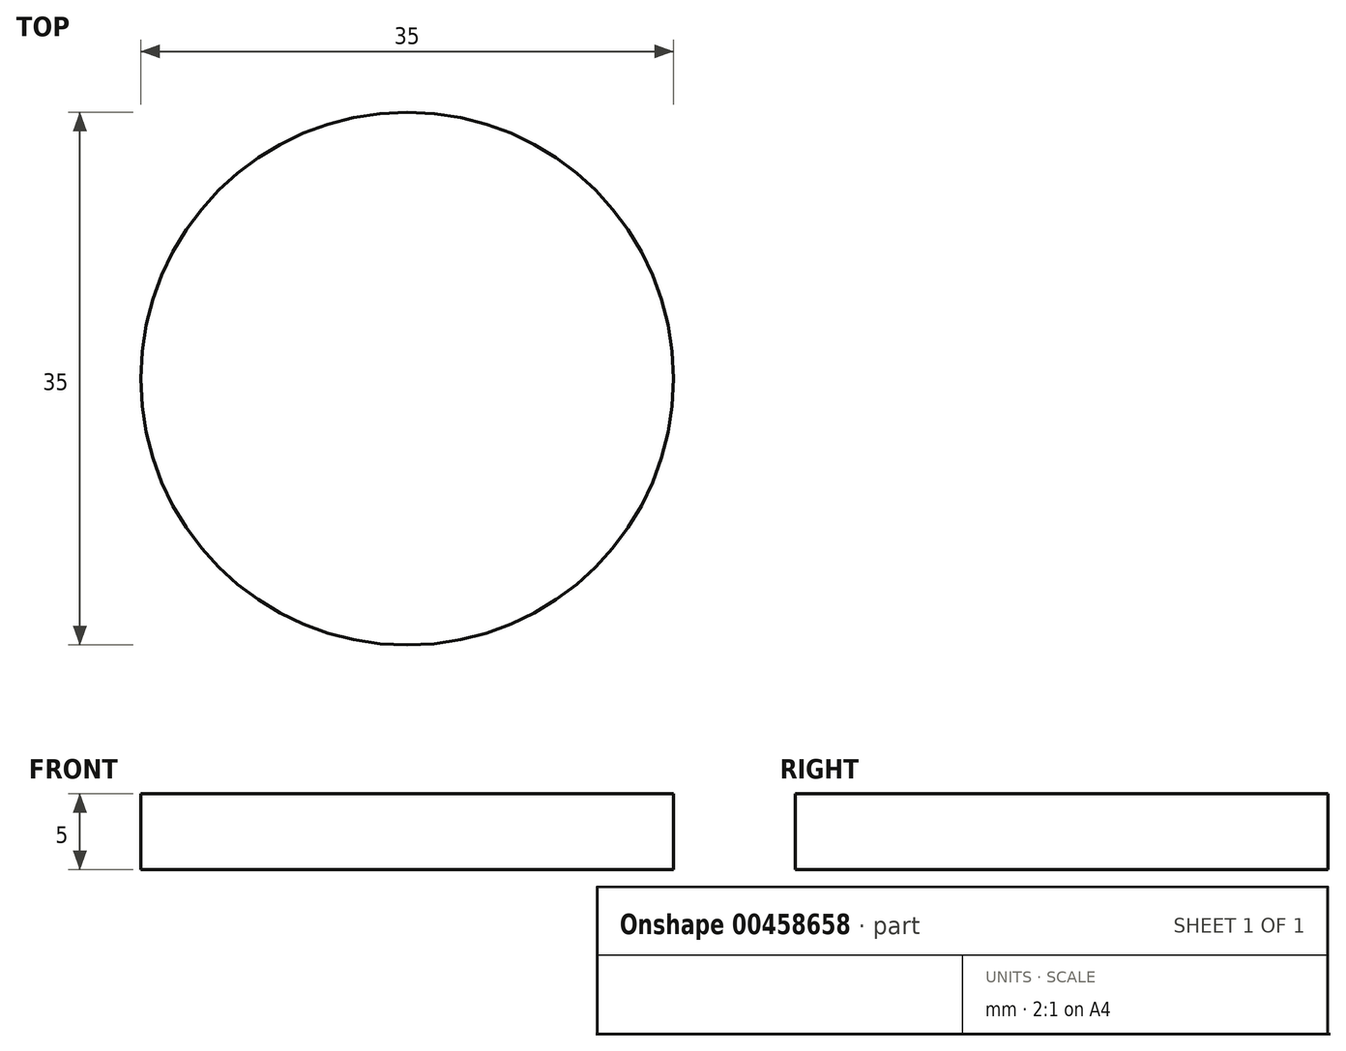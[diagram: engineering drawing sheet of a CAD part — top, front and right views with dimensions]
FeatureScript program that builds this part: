
annotation { "Feature Type Name" : "Feature", "Feature Type Description" : "" }
export const myFeature = defineFeature(function(context is Context, id is Id, definition is map)
    precondition{}
    {
        {
            var Q0;
            Q0=qCreatedBy(makeId("Top.planeOp"),FACE);
            var sketch = newSketch(context, id + "F0", { "sketchPlane" : qUnion([Q0])});
            skCircle(sketch, "E0", {"center": v(0, 0) * mm, "radius": 17.5 * mm});
            skSolve(sketch);
        }
        {
            var Q0;
            Q0=makeQuery(id+"F0.imprint","IMPRINT",FACE,{"disambiguationData":[TD([[makeQuery(id+"F0.imprint","IMPRINT",EDGE,{"derivedFrom":sQuery(id+"F0.wireOp",EDGE,"E0")}),1.0]])]});
            extrude(context, id + "F1", {"entities" : qUnion([Q0]), "depth" : 5 * mm});
        }
    });
